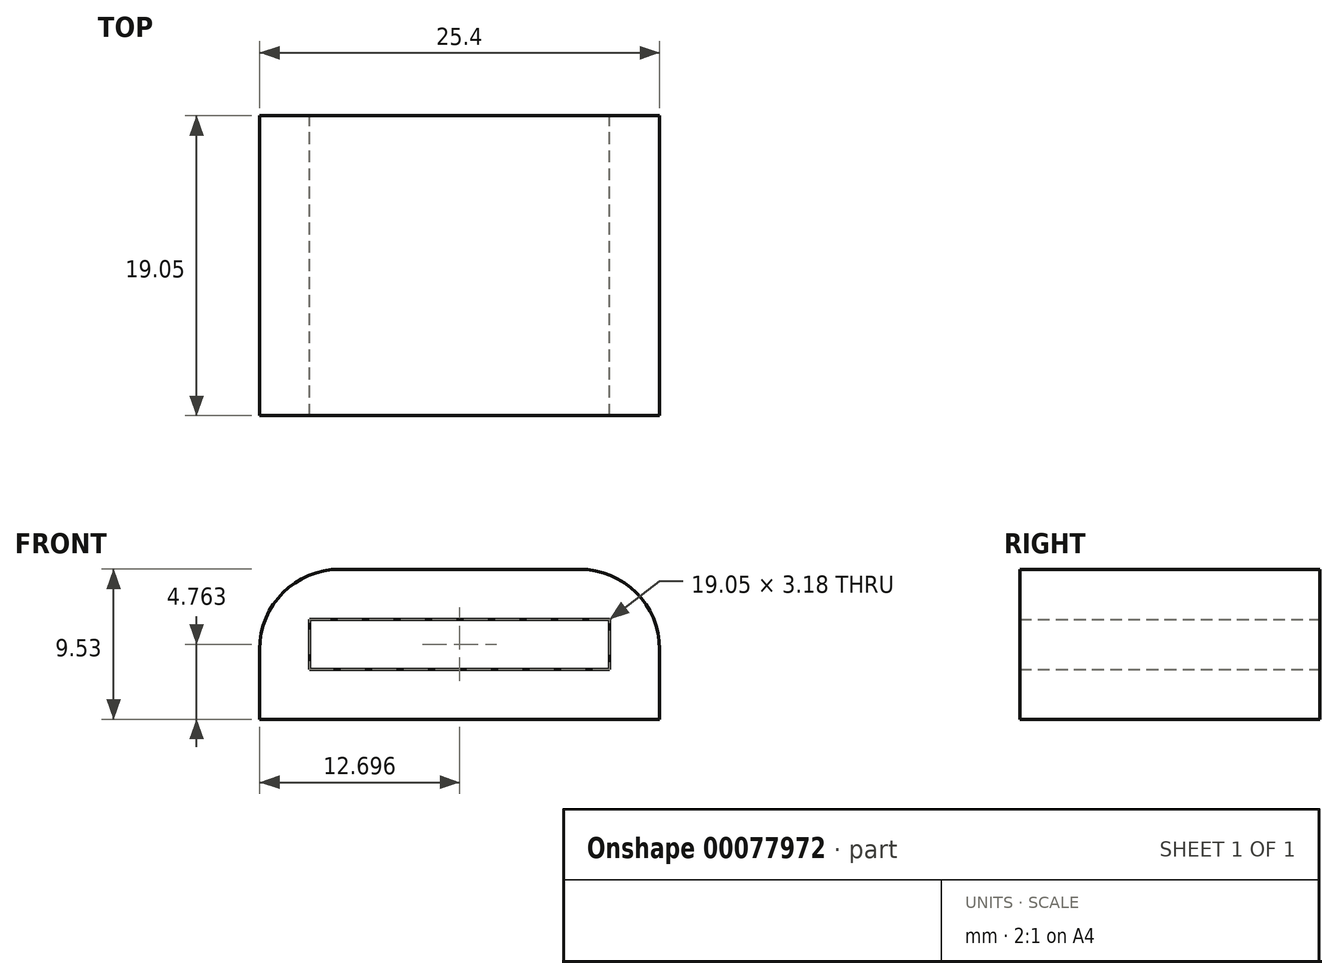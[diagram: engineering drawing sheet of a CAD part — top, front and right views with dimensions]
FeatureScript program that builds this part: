
annotation { "Feature Type Name" : "Feature", "Feature Type Description" : "" }
export const myFeature = defineFeature(function(context is Context, id is Id, definition is map)
    precondition{}
    {
        {
            var Q0;
            Q0=qCreatedBy(makeId("Front.planeOp"),FACE);
            var sketch = newSketch(context, id + "F0", { "sketchPlane" : qUnion([Q0])});
            skLineSegment(sketch, "E0.top", {"start": v(-44.68, 12.64) * mm, "end": v(-19.28, 12.64) * mm});
            skLineSegment(sketch, "E0.left", {"start": v(-44.68, 22.17) * mm, "end": v(-44.68, 12.64) * mm});
            skLineSegment(sketch, "E0.right", {"start": v(-19.28, 22.17) * mm, "end": v(-19.28, 12.64) * mm});
            skLineSegment(sketch, "E1.0", {"start": v(-41.5, 15.82) * mm, "end": v(-22.46, 15.82) * mm});
            skLineSegment(sketch, "E2.0", {"start": v(-41.5, 19) * mm, "end": v(-22.46, 19) * mm});
            skLineSegment(sketch, "E3.0", {"start": v(-41.5, 19) * mm, "end": v(-41.5, 15.82) * mm});
            skLineSegment(sketch, "E4.0", {"start": v(-22.46, 19) * mm, "end": v(-22.46, 15.82) * mm});
            skLineSegment(sketch, "E5.0", {"start": v(-44.68, 22.17) * mm, "end": v(-19.28, 22.17) * mm});
            skSolve(sketch);
        }
        {
            var Q0;
            Q0 = qSketchRegion(id + "F0", true);
            extrude(context, id + "F1", {"entities" : qUnion([Q0]), "depth" : 19.05 * mm});
        }
        {
            var Q0;
            Q0=makeQuery(id+"F1.opExtrude","SWEPT_EDGE",EDGE,{"disambiguationData":[OSD([sQuery(id+"F0.wireOp",EDGE,"E0.left"),sQuery(id+"F0.wireOp",EDGE,"E5.0")])]});
            var Q1;
            Q1=makeQuery(id+"F1.opExtrude","SWEPT_EDGE",EDGE,{"disambiguationData":[OSD([sQuery(id+"F0.wireOp",EDGE,"E0.right"),sQuery(id+"F0.wireOp",EDGE,"E5.0")])]});
            fillet(context, id + "F2", {"entities" : qUnion([Q0, Q1]), "radius" : 5.08 * mm, "tangentPropagation" : true, "allowEdgeOverflow" : false});
        }
    });
